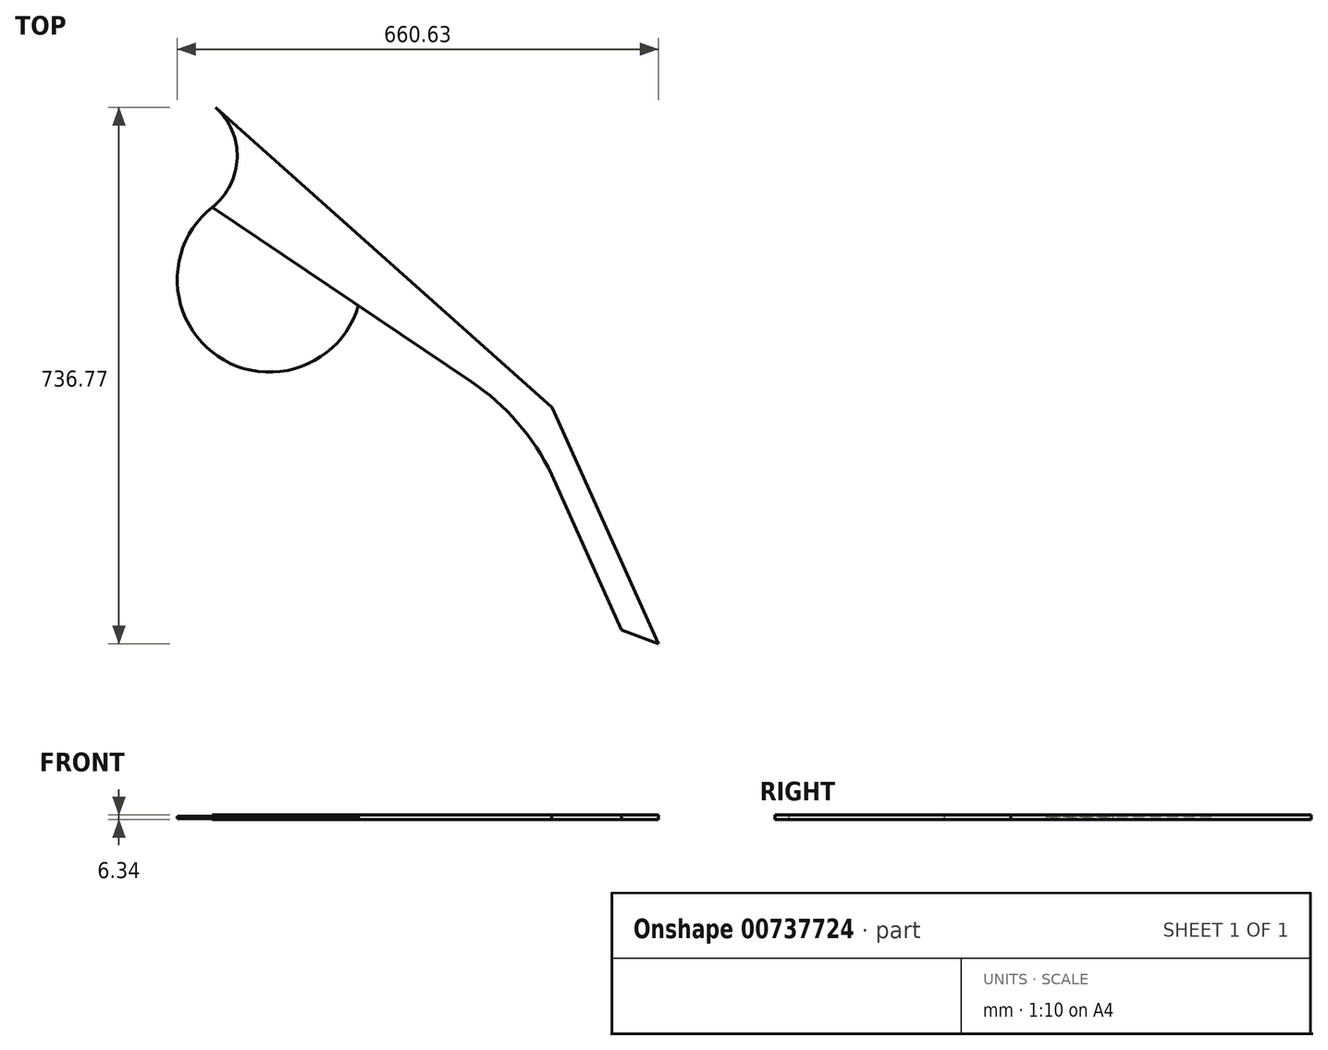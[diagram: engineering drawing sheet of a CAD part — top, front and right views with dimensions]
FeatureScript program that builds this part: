
annotation { "Feature Type Name" : "Feature", "Feature Type Description" : "" }
export const myFeature = defineFeature(function(context is Context, id is Id, definition is map)
    precondition{}
    {
        {
            var Q0;
            Q0=qCreatedBy(makeId("Top.planeOp"),FACE);
            var sketch = newSketch(context, id + "F0", { "sketchPlane" : qUnion([Q0])});
            skCircle(sketch, "E0", {"center": v(-161.5, 41.35) * mm, "radius": 127 * mm});
            skLineSegment(sketch, "E1", {"start": v(-76.96, 136.12) * mm, "end": v(226.33, -134.4) * mm});
            skLineSegment(sketch, "E2", {"start": v(226.33, -134.4) * mm, "end": v(372.14, -458.72) * mm});
            skLineSegment(sketch, "E3", {"start": v(115.38, -98.65) * mm, "end": v(-240.19, 141.03) * mm});
            skLineSegment(sketch, "E4", {"start": v(-76.96, 136.12) * mm, "end": v(-236.07, 278.05) * mm});
            skArc(sketch, "E5", {"start": v(-240.19, 141.03) * mm, "mid": v(-206.2, 208.58) * mm, "end": v(-236.07, 278.05) * mm});
            skLineSegment(sketch, "E6", {"start": v(225.84, -226.21) * mm, "end": v(321.77, -439.6) * mm});
            skLineSegment(sketch, "E7", {"start": v(321.77, -439.6) * mm, "end": v(372.14, -458.72) * mm});
            skPoint(sketch, "E8.end.orphan", {"position": v(191.58, -150.01) * mm});
            skArc(sketch, "E9", {"start": v(225.84, -226.21) * mm, "mid": v(179.08, -155.1) * mm, "end": v(115.38, -98.65) * mm});
            skSolve(sketch);
        }
        {
            var Q0;
            {var subQ0=sQuery(id+"F0.wireOp",EDGE,"E3");var subQ1=sQuery(id+"F0.wireOp",EDGE,"E0");var subQ3=makeQuery(id+"F0.imprint","INTERSECT",VERTEX,{"derivedFrom":[subQ1,subQ0]});Q0=makeQuery(id+"F0.imprint","IMPRINT",FACE,{"disambiguationData":[TD([[makeQuery(id+"F0.imprint","IMPRINT",EDGE,{"disambiguationData":[TD([[subQ3,1.0]])],"derivedFrom":subQ1}),1.0]])]});}
            var Q1;
            {var subQ0=sQuery(id+"F0.wireOp",EDGE,"E0");var subQ2=sQuery(id+"F0.wireOp",EDGE,"E3");var subQ4=makeQuery(id+"F0.imprint","INTERSECT",VERTEX,{"derivedFrom":[subQ0,subQ2]});Q1=makeQuery(id+"F0.imprint","IMPRINT",FACE,{"disambiguationData":[TD([[makeQuery(id+"F0.imprint","IMPRINT",EDGE,{"disambiguationData":[TD([[subQ4,-1.0]])],"derivedFrom":subQ0}),1.0]])]});}
            extrude(context, id + "F1", {"entities" : qUnion([Q0, Q1]), "depth" : 1.59 * mm, "offsetDistance" : 25.4 * mm, "hasSecondDirection" : true, "secondDirectionOppositeDirection" : true, "secondDirectionDepth" : 1.59 * mm});
        }
        {
            var Q0;
            {var subQ0=sQuery(id+"F0.wireOp",EDGE,"E4");Q0=makeQuery(id+"F0.imprint","IMPRINT",FACE,{"disambiguationData":[TD([[makeQuery(id+"F0.imprint","IMPRINT",EDGE,{"derivedFrom":subQ0}),1.0]])]});}
            var Q1;
            {var subQ4=sQuery(id+"F0.wireOp",EDGE,"E1");Q1=makeQuery(id+"F0.imprint","IMPRINT",FACE,{"disambiguationData":[TD([[makeQuery(id+"F0.imprint","IMPRINT",EDGE,{"derivedFrom":subQ4}),-1.0]])]});}
            var Q2;
            {var subQ0=sQuery(id+"F0.wireOp",EDGE,"E0");var subQ2=sQuery(id+"F0.wireOp",EDGE,"E3");var subQ4=makeQuery(id+"F0.imprint","INTERSECT",VERTEX,{"derivedFrom":[subQ0,subQ2]});Q2=makeQuery(id+"F0.imprint","IMPRINT",FACE,{"disambiguationData":[TD([[makeQuery(id+"F0.imprint","IMPRINT",EDGE,{"disambiguationData":[TD([[subQ4,-1.0]])],"derivedFrom":subQ0}),1.0]])]});}
            extrude(context, id + "F2", {"entities" : qUnion([Q0, Q1, Q2]), "operationType" : NewBodyOperationType.ADD, "depth" : 3.17 * mm, "offsetDistance" : 25.4 * mm, "hasSecondDirection" : true, "secondDirectionOppositeDirection" : true, "secondDirectionDepth" : 3.17 * mm});
        }
    });
